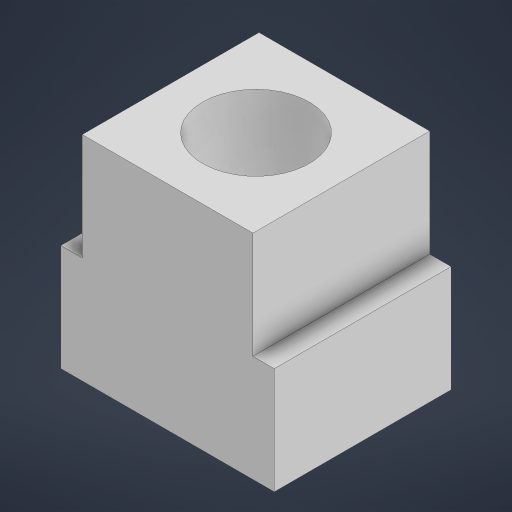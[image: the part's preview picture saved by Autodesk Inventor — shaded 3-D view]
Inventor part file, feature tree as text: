
AUTODESK INVENTOR PART (.ipt)
format: ipt  version: 2024.3 (Build 283343000, 343)  size: 172,032 bytes
history: native  units: in
note: dims shown in document units (in); Inventor stores cm internally (conversion verified against a paired STEP export)
features: extrude x2, sketch x2
ambient origin geometry x8: Origin, YZ Plane, XZ Plane, XY Plane, X Axis, Y Axis, Z Axis, Center Point
bodies: Solid1 (feature_tree)
feature tree (4):
  extrude  "Extrusion1"  Depth=0.3937in
  extrude  "Extrusion2"  Depth=0.1969in TaperAngle=180.0deg
  sketch  "Sketch2"  dims[d0=0.3937in d1=0.3937in]
  sketch  "Sketch3"  dims[d2=0.1969in d3=0.7874in d5=180.0deg d7=0.3937in d8=0.0in d9=0.0394in d10=0.7874in d12=180.0deg d16=0.1969in d17=0.0in d18=0.0197in d19=0.0344in]
